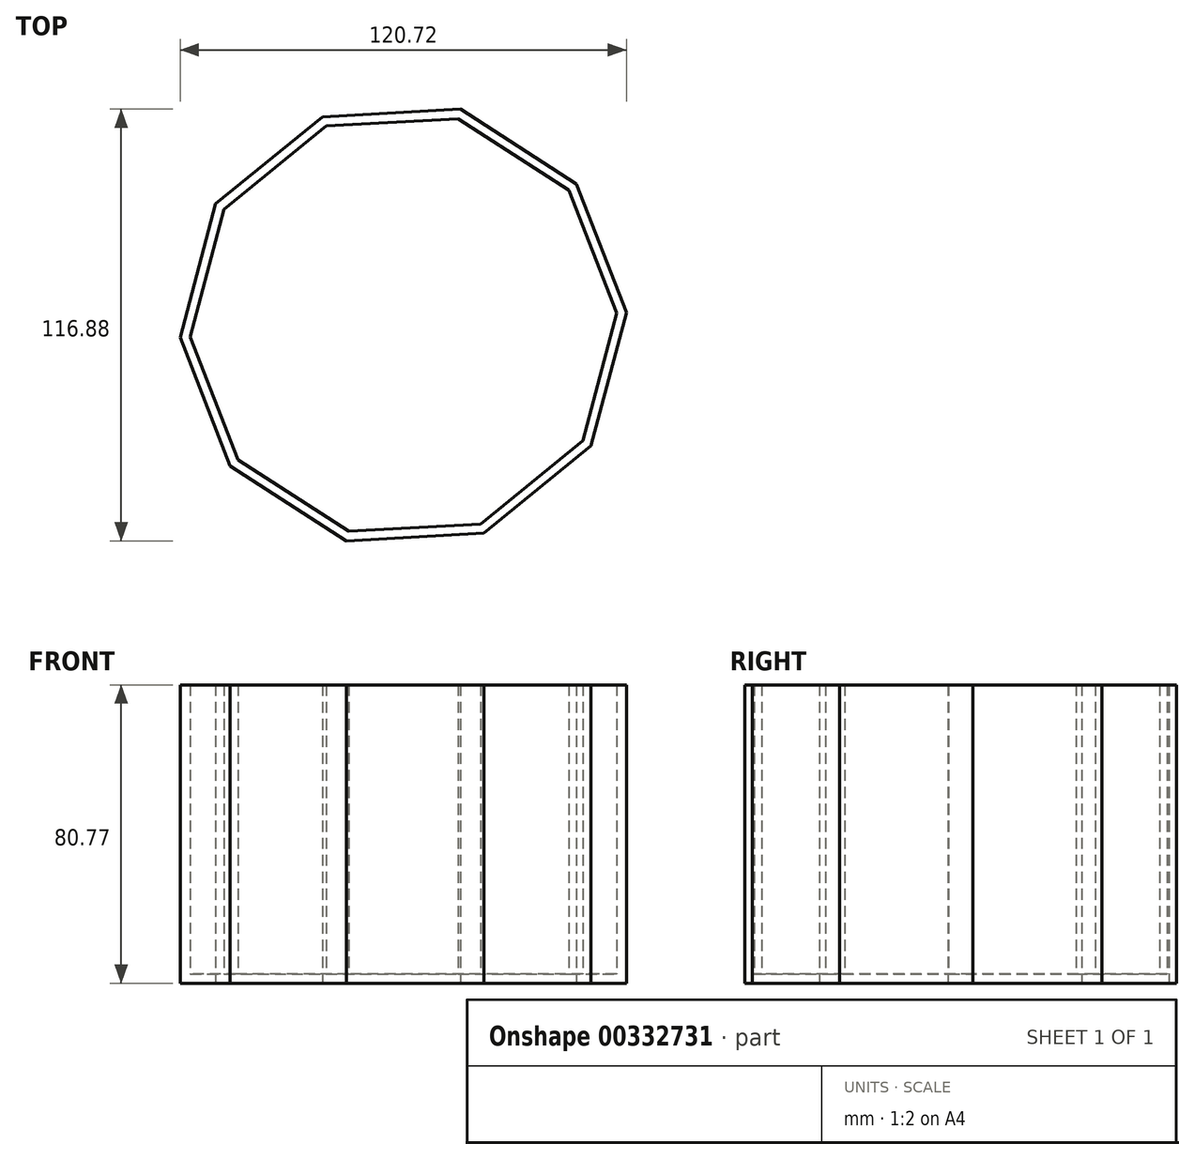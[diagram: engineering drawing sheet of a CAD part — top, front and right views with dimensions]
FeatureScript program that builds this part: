
annotation { "Feature Type Name" : "Feature", "Feature Type Description" : "" }
export const myFeature = defineFeature(function(context is Context, id is Id, definition is map)
    precondition{}
    {
        {
            var Q0;
            Q0=qCreatedBy(makeId("Top.planeOp"),FACE);
            var sketch = newSketch(context, id + "F0", { "sketchPlane" : qUnion([Q0])});
            skCircle(sketch, "E0.cCircle", {"center": v(0, 0) * mm, "radius": 57.5 * mm, "construction": true});
            skLineSegment(sketch, "E0.0", {"start": v(-50.8, 32.76) * mm, "end": v(-21.85, 56.36) * mm});
            skLineSegment(sketch, "E0.1", {"start": v(-21.85, 56.36) * mm, "end": v(15.45, 58.44) * mm});
            skLineSegment(sketch, "E0.2", {"start": v(15.45, 58.44) * mm, "end": v(46.85, 38.2) * mm});
            skLineSegment(sketch, "E0.3", {"start": v(46.85, 38.2) * mm, "end": v(60.36, 3.36) * mm});
            skLineSegment(sketch, "E0.4", {"start": v(60.36, 3.36) * mm, "end": v(50.8, -32.76) * mm});
            skLineSegment(sketch, "E0.5", {"start": v(50.8, -32.76) * mm, "end": v(21.85, -56.36) * mm});
            skLineSegment(sketch, "E0.6", {"start": v(21.85, -56.36) * mm, "end": v(-15.45, -58.44) * mm});
            skLineSegment(sketch, "E0.7", {"start": v(-15.45, -58.44) * mm, "end": v(-46.85, -38.2) * mm});
            skLineSegment(sketch, "E0.8", {"start": v(-46.85, -38.2) * mm, "end": v(-60.36, -3.36) * mm});
            skLineSegment(sketch, "E0.9", {"start": v(-60.36, -3.36) * mm, "end": v(-50.8, 32.76) * mm});
            skPoint(sketch, "E0.0.midPoint", {"position": v(-36.33, 44.56) * mm});
            skSolve(sketch);
        }
        {
            var Q0;
            Q0 = qSketchRegion(id + "F0", true);
            extrude(context, id + "F1", {"entities" : qUnion([Q0]), "depth" : 80.77 * mm});
        }
        {
            var Q0;
            Q0=makeQuery(id+"F1.opExtrude","CAP_FACE",FACE,{"disambiguationData":[OSD([sQuery(id+"F0.wireOp",EDGE,"E0.0"),sQuery(id+"F0.wireOp",EDGE,"E0.1"),sQuery(id+"F0.wireOp",EDGE,"E0.2"),sQuery(id+"F0.wireOp",EDGE,"E0.3"),sQuery(id+"F0.wireOp",EDGE,"E0.4"),sQuery(id+"F0.wireOp",EDGE,"E0.5"),sQuery(id+"F0.wireOp",EDGE,"E0.6"),sQuery(id+"F0.wireOp",EDGE,"E0.7"),sQuery(id+"F0.wireOp",EDGE,"E0.8"),sQuery(id+"F0.wireOp",EDGE,"E0.9")])],"isStart":false});
            shell(context, id + "F2", {"entities" : qUnion([Q0]), "thickness" : 2.54 * mm});
        }
    });
